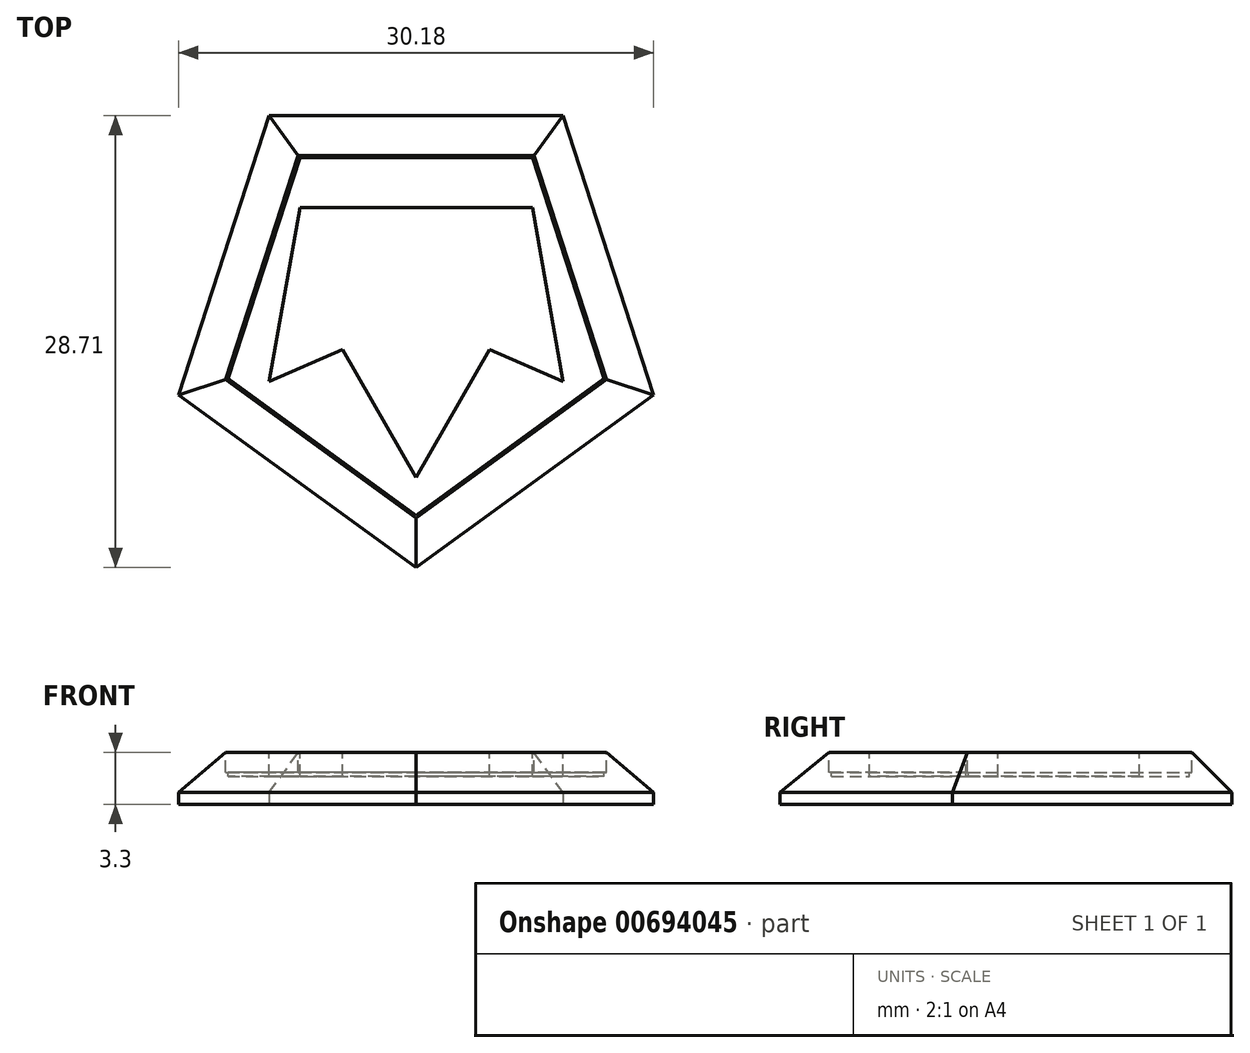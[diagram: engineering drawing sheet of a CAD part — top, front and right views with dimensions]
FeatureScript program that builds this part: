
annotation { "Feature Type Name" : "Feature", "Feature Type Description" : "" }
export const myFeature = defineFeature(function(context is Context, id is Id, definition is map)
    precondition{}
    {
        {
            var Q0;
            Q0=qCreatedBy(makeId("Top.planeOp"),FACE);
            var sketch = newSketch(context, id + "F0", { "sketchPlane" : qUnion([Q0])});
            skCircle(sketch, "E0.cCircle", {"center": v(0, 0) * mm, "radius": 12.84 * mm, "construction": true});
            skLineSegment(sketch, "E0.0", {"start": v(-9.33, 12.84) * mm, "end": v(9.33, 12.84) * mm});
            skLineSegment(sketch, "E0.1", {"start": v(9.33, 12.84) * mm, "end": v(15.09, -4.9) * mm});
            skLineSegment(sketch, "E0.2", {"start": v(15.09, -4.9) * mm, "end": v(0, -15.87) * mm});
            skLineSegment(sketch, "E0.3", {"start": v(0, -15.87) * mm, "end": v(-15.09, -4.9) * mm});
            skLineSegment(sketch, "E0.4", {"start": v(-15.09, -4.9) * mm, "end": v(-9.33, 12.84) * mm});
            skPoint(sketch, "E0.0.midPoint", {"position": v(0, 12.84) * mm});
            skSolve(sketch);
        }
        {
            var Q0;
            Q0=makeQuery(id+"F0.imprint","IMPRINT",FACE,{"disambiguationData":[TD([[makeQuery(id+"F0.imprint","IMPRINT",EDGE,{"derivedFrom":sQuery(id+"F0.wireOp",EDGE,"E0.0")}),-1.0]])]});
            extrude(context, id + "F1", {"entities" : qUnion([Q0]), "depth" : 3.3 * mm, "offsetDistance" : 25.4 * mm});
        }
        {
            var Q0;
            Q0=makeQuery(id+"F1.opExtrude","CAP_FACE",FACE,{"disambiguationData":[OSD([sQuery(id+"F0.wireOp",EDGE,"E0.0"),sQuery(id+"F0.wireOp",EDGE,"E0.1"),sQuery(id+"F0.wireOp",EDGE,"E0.2"),sQuery(id+"F0.wireOp",EDGE,"E0.3"),sQuery(id+"F0.wireOp",EDGE,"E0.4")])],"isStart":false});
            var sketch = newSketch(context, id + "F2", { "sketchPlane" : qUnion([Q0])});
            skCircle(sketch, "E1.cCircle", {"center": v(0, 0) * mm, "radius": 10.16 * mm, "construction": true});
            skPoint(sketch, "E1.cCircle.perimeterSnap0", {"position": v(0, 12.84) * mm});
            skLineSegment(sketch, "E1.0", {"start": v(-7.38, 10.16) * mm, "end": v(7.38, 10.16) * mm});
            skLineSegment(sketch, "E1.1", {"start": v(7.38, 10.16) * mm, "end": v(11.95, -3.88) * mm});
            skLineSegment(sketch, "E1.2", {"start": v(11.95, -3.88) * mm, "end": v(0, -12.56) * mm});
            skLineSegment(sketch, "E1.3", {"start": v(0, -12.56) * mm, "end": v(-11.95, -3.88) * mm});
            skLineSegment(sketch, "E1.4", {"start": v(-11.95, -3.88) * mm, "end": v(-7.38, 10.16) * mm});
            skPoint(sketch, "E1.0.midPoint", {"position": v(0, 10.16) * mm});
            skPoint(sketch, "E1.0.midPoint.positionSnap0", {"position": v(0, 12.84) * mm});
            skLineSegment(sketch, "E2", {"start": v(-7.38, 6.98) * mm, "end": v(-9.33, -4.04) * mm});
            skLineSegment(sketch, "E3", {"start": v(-9.33, -4.04) * mm, "end": v(0, 0) * mm});
            skLineSegment(sketch, "E4", {"start": v(7.38, 6.98) * mm, "end": v(9.33, -4.04) * mm});
            skLineSegment(sketch, "E5", {"start": v(9.33, -4.04) * mm, "end": v(0, 0) * mm});
            skLineSegment(sketch, "E6", {"start": v(4.66, -2.02) * mm, "end": v(0, -10.16) * mm});
            skLineSegment(sketch, "E7", {"start": v(0, -10.16) * mm, "end": v(-4.66, -2.02) * mm});
            skLineSegment(sketch, "E8", {"start": v(-4.66, -2.02) * mm, "end": v(0, 0) * mm});
            skPoint(sketch, "E9.endSnap0", {"position": v(-9.67, 3.14) * mm});
            skLineSegment(sketch, "E10", {"start": v(0, 6.98) * mm, "end": v(7.38, 6.98) * mm});
            skLineSegment(sketch, "E11", {"start": v(0, 6.98) * mm, "end": v(-7.38, 6.98) * mm});
            skSolve(sketch);
        }
        {
            var Q0;
            Q0 = qSketchRegion(id + "F2", true);
            extrude(context, id + "F3", {"entities" : qUnion([Q0]), "operationType" : NewBodyOperationType.REMOVE, "oppositeDirection" : true, "depth" : 1.52 * mm, "offsetDistance" : 25.4 * mm});
        }
        {
            var Q0;
            Q0=makeQuery(id+"F1.opExtrude","CAP_EDGE",EDGE,{"disambiguationData":[OSD([sQuery(id+"F0.wireOp",EDGE,"E0.2")])],"isStart":false});
            var Q1;
            Q1=makeQuery(id+"F1.opExtrude","CAP_EDGE",EDGE,{"disambiguationData":[OSD([sQuery(id+"F0.wireOp",EDGE,"E0.3")])],"isStart":false});
            var Q2;
            Q2=makeQuery(id+"F1.opExtrude","CAP_EDGE",EDGE,{"disambiguationData":[OSD([sQuery(id+"F0.wireOp",EDGE,"E0.4")])],"isStart":false});
            var Q3;
            Q3=makeQuery(id+"F1.opExtrude","CAP_EDGE",EDGE,{"disambiguationData":[OSD([sQuery(id+"F0.wireOp",EDGE,"E0.0")])],"isStart":false});
            var Q4;
            Q4=makeQuery(id+"F1.opExtrude","CAP_EDGE",EDGE,{"disambiguationData":[OSD([sQuery(id+"F0.wireOp",EDGE,"E0.1")])],"isStart":false});
            chamfer(context, id + "F4", {"entities" : qUnion([Q0, Q1, Q2, Q3, Q4]), "width" : 2.54 * mm, "tangentPropagation" : true});
        }
        {
            var Q0;
            {var subQ0=sQuery(id+"F0.wireOp",EDGE,"E0.2");var subQ1=sQuery(id+"F0.wireOp",EDGE,"E0.1");var subQ2=sQuery(id+"F0.wireOp",EDGE,"E0.3");var subQ3=sQuery(id+"F0.wireOp",EDGE,"E0.0");var subQ4=sQuery(id+"F0.wireOp",EDGE,"E0.4");Q0=makeQuery(id+"F3.boolean.opBoolean","SPLIT",FACE,{"disambiguationData":[TD([makeQuery(id+"F1.opExtrude","SWEPT_FACE",FACE,{"disambiguationData":[OSD([subQ3])]})])],"derivedFrom":makeQuery(id+"F1.opExtrude","CAP_FACE",FACE,{"disambiguationData":[OSD([subQ3,subQ1,subQ0,subQ2,subQ4])],"isStart":false})});}
            extrude(context, id + "F5", {"entities" : qUnion([Q0]), "operationType" : NewBodyOperationType.REMOVE, "oppositeDirection" : true, "depth" : 1.27 * mm, "offsetDistance" : 25.4 * mm});
        }
    });
